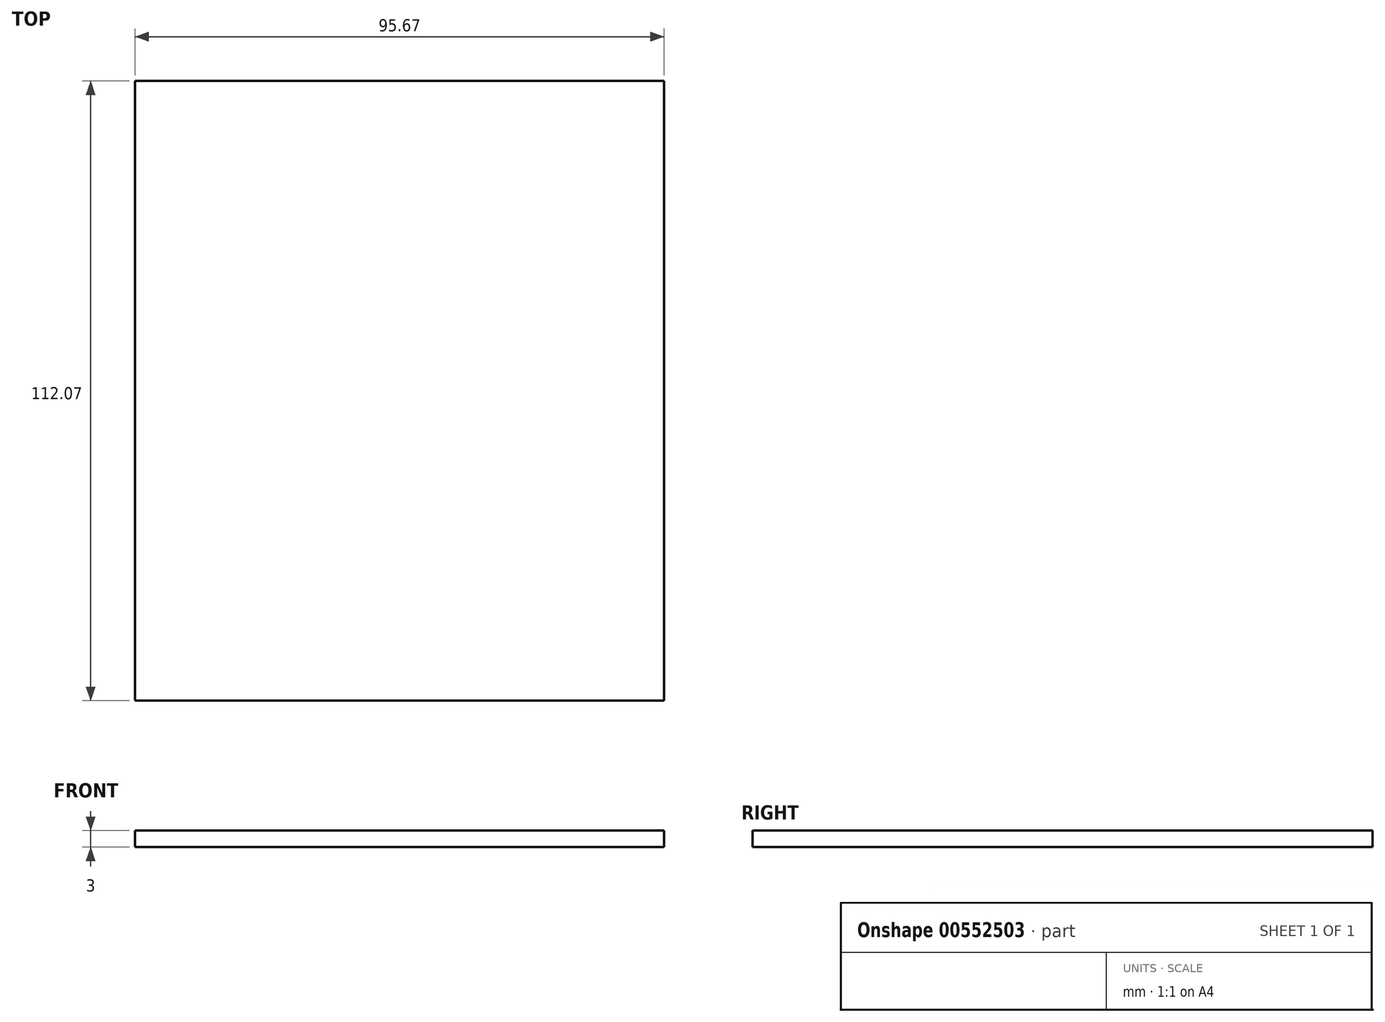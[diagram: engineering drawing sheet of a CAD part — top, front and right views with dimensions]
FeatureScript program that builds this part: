
annotation { "Feature Type Name" : "Feature", "Feature Type Description" : "" }
export const myFeature = defineFeature(function(context is Context, id is Id, definition is map)
    precondition{}
    {
        {
            var Q0;
            Q0=qCreatedBy(makeId("Top.planeOp"),FACE);
            var sketch = newSketch(context, id + "F0", { "sketchPlane" : qUnion([Q0])});
            skLineSegment(sketch, "E0.bottom", {"start": v(15.03, 12.57) * mm, "end": v(110.7, 12.57) * mm});
            skLineSegment(sketch, "E0.top", {"start": v(15.03, 124.64) * mm, "end": v(110.7, 124.64) * mm});
            skLineSegment(sketch, "E0.left", {"start": v(15.03, 12.57) * mm, "end": v(15.03, 124.64) * mm});
            skLineSegment(sketch, "E0.right", {"start": v(110.7, 12.57) * mm, "end": v(110.7, 124.64) * mm});
            skSolve(sketch);
        }
        {
            var Q0;
            Q0=makeQuery(id+"F0.imprint","IMPRINT",FACE,{"disambiguationData":[TD([[makeQuery(id+"F0.imprint","IMPRINT",EDGE,{"derivedFrom":sQuery(id+"F0.wireOp",EDGE,"E0.bottom")}),1.0]])]});
            extrude(context, id + "F1", {"entities" : qUnion([Q0]), "depth" : 3 * mm, "offsetDistance" : 25.4 * mm});
        }
    });
